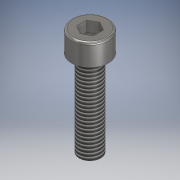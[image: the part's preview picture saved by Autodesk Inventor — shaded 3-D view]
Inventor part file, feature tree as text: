
AUTODESK INVENTOR PART (.ipt)
format: ipt  version: 2019 (Build 230136000, 136)  size: 134,144 bytes
history: native  units: mm
features: other x3, extrude x2, fillet x1
ambient origin geometry x8: Origin, YZ Plane, XZ Plane, XY Plane, X Axis, Y Axis, Z Axis, Center Point
bodies: Solid1 (feature_tree), Body (feature_tree)
feature tree (6):
  extrude  "Cap"  Depth=8.5mm
  extrude  "Key Socket Cutout"  Depth=5.0mm TaperAngle=0.0deg
  fillet  "Cap Fillet"  Radius=4.0mm
  other  "Cap Cross Section"
  other  "Key Socket Cutout Outline"
  other  "Body Cross Section"
